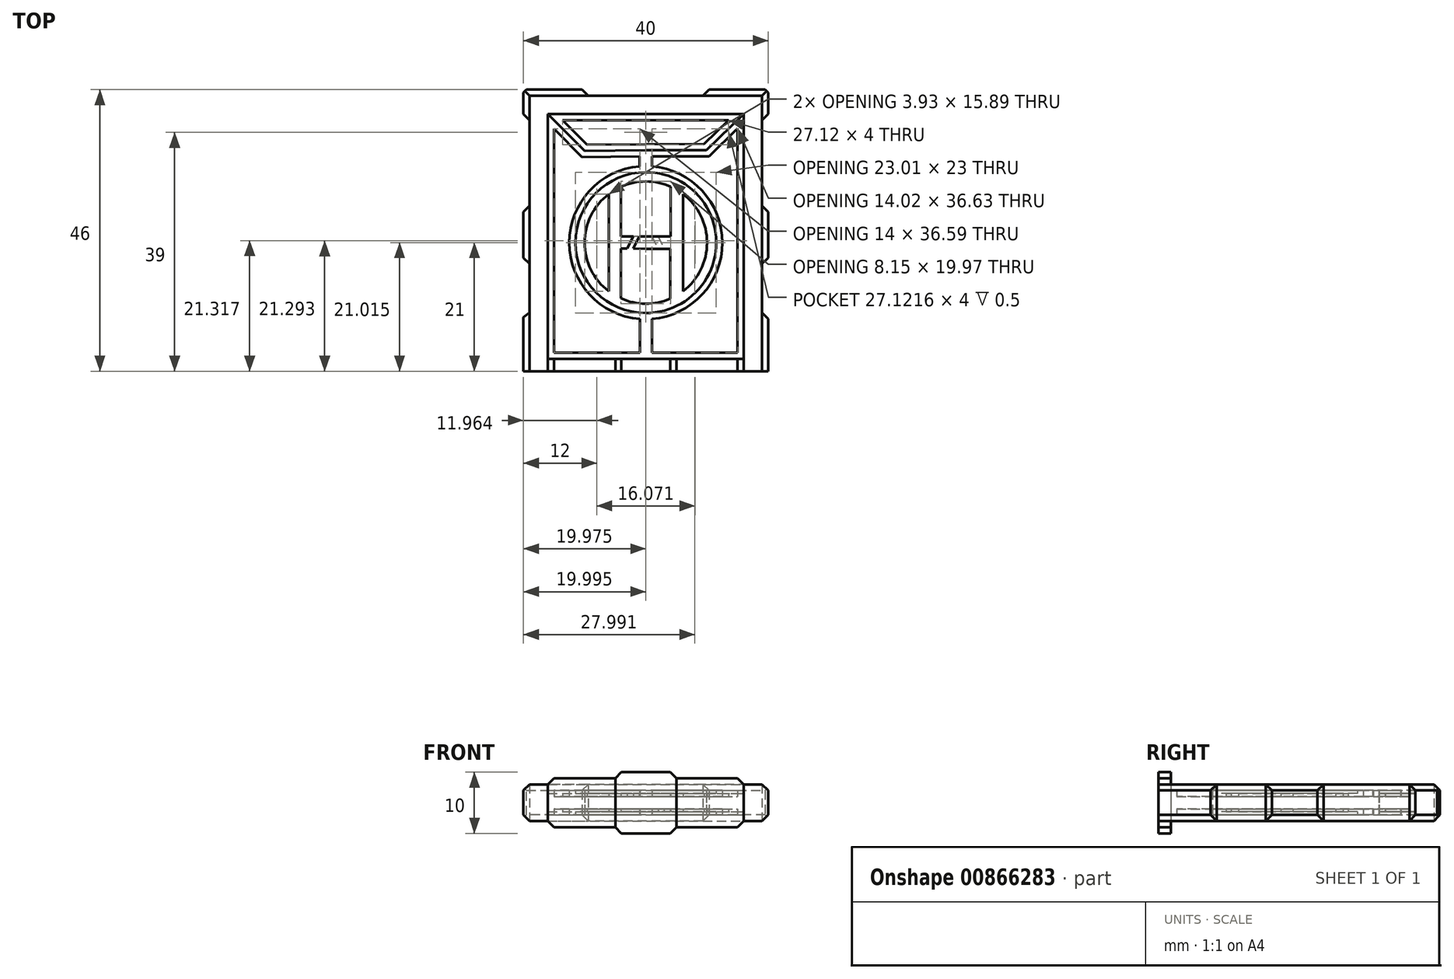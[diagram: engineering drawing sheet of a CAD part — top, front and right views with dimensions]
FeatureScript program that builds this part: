
annotation { "Feature Type Name" : "Feature", "Feature Type Description" : "" }
export const myFeature = defineFeature(function(context is Context, id is Id, definition is map)
    precondition{}
    {
        {
            var Q0;
            Q0=qCreatedBy(makeId("Top.planeOp"),FACE);
            var sketch = newSketch(context, id + "F0", { "sketchPlane" : qUnion([Q0])});
            skLineSegment(sketch, "E0.bottom", {"start": v(-16, 21) * mm, "end": v(16, 21) * mm});
            skPoint(sketch, "E0.middle", {"position": v(0, 0) * mm});
            skLineSegment(sketch, "E1", {"start": v(16, -21) * mm, "end": v(20, -21) * mm});
            skLineSegment(sketch, "E2", {"start": v(-16, -21) * mm, "end": v(-20, -21) * mm});
            skLineSegment(sketch, "E3", {"start": v(9.91, 15.09) * mm, "end": v(16, 21) * mm});
            skLineSegment(sketch, "E4", {"start": v(-16, 21) * mm, "end": v(-10, 15) * mm});
            skLineSegment(sketch, "E5", {"start": v(6.07, 1) * mm, "end": v(6.07, 7.95) * mm});
            skLineSegment(sketch, "E6", {"start": v(6.07, 1) * mm, "end": v(6.07, -7.95) * mm});
            skLineSegment(sketch, "E7", {"start": v(-6.07, 1) * mm, "end": v(-6.07, 7.95) * mm});
            skLineSegment(sketch, "E8", {"start": v(-6.07, 1) * mm, "end": v(-6.07, -7.95) * mm});
            skLineSegment(sketch, "E9", {"start": v(-4.07, 1) * mm, "end": v(-4.07, 9.13) * mm});
            skLineSegment(sketch, "E10", {"start": v(-4.08, -0.97) * mm, "end": v(-4.08, -9.13) * mm});
            skLineSegment(sketch, "E11", {"start": v(4.07, 1) * mm, "end": v(4.07, 9.13) * mm});
            skLineSegment(sketch, "E12", {"start": v(4, -1) * mm, "end": v(-0.08, -1) * mm});
            skLineSegment(sketch, "E13", {"start": v(4.07, 1) * mm, "end": v(0, 1) * mm});
            skLineSegment(sketch, "E14", {"start": v(4, -1) * mm, "end": v(4, -9.13) * mm});
            skLineSegment(sketch, "E15", {"start": v(-4.08, -0.97) * mm, "end": v(-3.08, -0.98) * mm});
            skLineSegment(sketch, "E16", {"start": v(-4.07, 1) * mm, "end": v(-2.08, 1) * mm});
            skLineSegment(sketch, "E17", {"start": v(-3.08, -0.98) * mm, "end": v(-2.08, 1) * mm});
            skLineSegment(sketch, "E18", {"start": v(-2.08, -0.98) * mm, "end": v(-1.08, 1) * mm});
            skLineSegment(sketch, "E19", {"start": v(-2.08, -0.98) * mm, "end": v(-0.08, -1) * mm});
            skLineSegment(sketch, "E20", {"start": v(-1.08, 1) * mm, "end": v(0, 1) * mm});
            skLineSegment(sketch, "E21.0", {"start": v(-13.59, 20) * mm, "end": v(-9.59, 16) * mm});
            skLineSegment(sketch, "E21.1", {"start": v(-13.59, 20) * mm, "end": v(13.54, 20) * mm});
            skLineSegment(sketch, "E21.2", {"start": v(9.51, 16.1) * mm, "end": v(13.54, 20) * mm});
            skLineSegment(sketch, "E21.3", {"start": v(-9.59, 16) * mm, "end": v(9.51, 16.1) * mm});
            skLineSegment(sketch, "E22", {"start": v(-0.02, 15.09) * mm, "end": v(-0.02, 11.5) * mm});
            skArc(sketch, "E23", {"start": v(-0.02, 11.5) * mm, "mid": v(11.5, 0) * mm, "end": v(0, -11.5) * mm});
            skArc(sketch, "E24", {"start": v(0, -11.5) * mm, "mid": v(-11.5, 0) * mm, "end": v(-0.02, 11.5) * mm});
            skLineSegment(sketch, "E25", {"start": v(-0.02, 15.09) * mm, "end": v(-10, 15) * mm});
            skLineSegment(sketch, "E26", {"start": v(-0.02, 15.09) * mm, "end": v(9.91, 15.09) * mm});
            skArc(sketch, "E27", {"start": v(-4.07, 9.13) * mm, "mid": v(0, 10) * mm, "end": v(4.07, 9.13) * mm});
            skArc(sketch, "E28", {"start": v(6.07, 7.95) * mm, "mid": v(10, 0) * mm, "end": v(6.07, -7.95) * mm});
            skArc(sketch, "E29", {"start": v(4, -9.13) * mm, "mid": v(-0.05, -9.97) * mm, "end": v(-4.08, -9.1) * mm});
            skArc(sketch, "E30", {"start": v(-6.07, -7.95) * mm, "mid": v(-10, 0) * mm, "end": v(-6.07, 7.95) * mm});
            skLineSegment(sketch, "E31", {"start": v(0, -11.5) * mm, "end": v(0, -19) * mm});
            skLineSegment(sketch, "E32", {"start": v(0, -19) * mm, "end": v(16, -19) * mm});
            skLineSegment(sketch, "E33", {"start": v(0, -19) * mm, "end": v(-16, -19) * mm});
            skLineSegment(sketch, "E34", {"start": v(16, -19) * mm, "end": v(16, -21) * mm});
            skLineSegment(sketch, "E35", {"start": v(16, -19) * mm, "end": v(16, 21) * mm});
            skLineSegment(sketch, "E36", {"start": v(-16, -21) * mm, "end": v(-16, -19) * mm});
            skLineSegment(sketch, "E37", {"start": v(-16, -19) * mm, "end": v(-16, 21) * mm});
            skLineSegment(sketch, "E38.0", {"start": v(1, -12.46) * mm, "end": v(1, -18) * mm});
            skArc(sketch, "E38.1", {"start": v(0.98, 12.46) * mm, "mid": v(12.5, 0) * mm, "end": v(1, -12.46) * mm});
            skLineSegment(sketch, "E38.2", {"start": v(15, -18) * mm, "end": v(15, 18.63) * mm});
            skLineSegment(sketch, "E38.3", {"start": v(10.32, 14.09) * mm, "end": v(15, 18.63) * mm});
            skLineSegment(sketch, "E38.4", {"start": v(0.98, 14.09) * mm, "end": v(10.32, 14.09) * mm});
            skLineSegment(sketch, "E38.5", {"start": v(1, -18) * mm, "end": v(15, -18) * mm});
            skLineSegment(sketch, "E38.6", {"start": v(0.98, 14.09) * mm, "end": v(0.98, 12.46) * mm});
            skLineSegment(sketch, "E39.0", {"start": v(-1, -12.46) * mm, "end": v(-1, -18) * mm});
            skArc(sketch, "E39.1", {"start": v(-1, -12.46) * mm, "mid": v(-12.5, 0) * mm, "end": v(-1.02, 12.46) * mm});
            skLineSegment(sketch, "E39.2", {"start": v(-15, -18) * mm, "end": v(-15, 18.59) * mm});
            skLineSegment(sketch, "E39.3", {"start": v(-15, 18.59) * mm, "end": v(-10.41, 14) * mm});
            skLineSegment(sketch, "E39.4", {"start": v(-1.02, 14.08) * mm, "end": v(-10.41, 14) * mm});
            skLineSegment(sketch, "E39.5", {"start": v(-1, -18) * mm, "end": v(-15, -18) * mm});
            skLineSegment(sketch, "E39.6", {"start": v(-1.02, 14.08) * mm, "end": v(-1.02, 12.46) * mm});
            skLineSegment(sketch, "E40", {"start": v(20, 25) * mm, "end": v(20, 21) * mm});
            skLineSegment(sketch, "E41", {"start": v(20, -12.46) * mm, "end": v(20, -21) * mm});
            skLineSegment(sketch, "E42", {"start": v(-20, -21) * mm, "end": v(-20, -12.2) * mm});
            skLineSegment(sketch, "E43", {"start": v(-20, 21) * mm, "end": v(-20, 25) * mm});
            skLineSegment(sketch, "E44", {"start": v(10.32, 25) * mm, "end": v(20, 25) * mm});
            skLineSegment(sketch, "E45", {"start": v(-10.41, 25) * mm, "end": v(-20, 25) * mm});
            skLineSegment(sketch, "E46", {"start": v(-10.41, 25) * mm, "end": v(-9.41, 24) * mm});
            skLineSegment(sketch, "E47", {"start": v(9.32, 24) * mm, "end": v(-9.41, 24) * mm});
            skLineSegment(sketch, "E48", {"start": v(9.32, 24) * mm, "end": v(10.32, 25) * mm});
            skLineSegment(sketch, "E49", {"start": v(20, 21) * mm, "end": v(19, 20) * mm});
            skLineSegment(sketch, "E50", {"start": v(19, -11.46) * mm, "end": v(20, -12.46) * mm});
            skLineSegment(sketch, "E51", {"start": v(-20, -12.2) * mm, "end": v(-19, -11.46) * mm});
            skLineSegment(sketch, "E52", {"start": v(-20, 21) * mm, "end": v(-19, 20) * mm});
            skLineSegment(sketch, "E53", {"start": v(19, -11.46) * mm, "end": v(19, -3.46) * mm});
            skLineSegment(sketch, "E54", {"start": v(20, -2.46) * mm, "end": v(19, -3.46) * mm});
            skLineSegment(sketch, "E55", {"start": v(20, 5) * mm, "end": v(19, 6) * mm});
            skLineSegment(sketch, "E56", {"start": v(20, -2.46) * mm, "end": v(20, 5) * mm});
            skLineSegment(sketch, "E57", {"start": v(19, 6) * mm, "end": v(19, 20) * mm});
            skLineSegment(sketch, "E58", {"start": v(-19, -11.46) * mm, "end": v(-19, -3.46) * mm});
            skLineSegment(sketch, "E59", {"start": v(-20, 5) * mm, "end": v(-19, 6) * mm});
            skLineSegment(sketch, "E60", {"start": v(-20, -2.46) * mm, "end": v(-19, -3.46) * mm});
            skLineSegment(sketch, "E61", {"start": v(-20, 5) * mm, "end": v(-20, -2.46) * mm});
            skLineSegment(sketch, "E62", {"start": v(-19, 6) * mm, "end": v(-19, 20) * mm});
            skLineSegment(sketch, "E63", {"start": v(-16, -21) * mm, "end": v(-14, -21) * mm});
            skLineSegment(sketch, "E64", {"start": v(14, -21) * mm, "end": v(16, -21) * mm});
            skLineSegment(sketch, "E65", {"start": v(-14, -21) * mm, "end": v(14, -21) * mm});
            skLineSegment(sketch, "E66", {"start": v(0, -21) * mm, "end": v(5, -21) * mm});
            skLineSegment(sketch, "E67", {"start": v(0, -21) * mm, "end": v(-5, -21) * mm});
            skLineSegment(sketch, "E68", {"start": v(-5, -21) * mm, "end": v(-5, -19) * mm});
            skLineSegment(sketch, "E69", {"start": v(5, -21) * mm, "end": v(5, -19) * mm});
            skLineSegment(sketch, "E70", {"start": v(-1.08, 1) * mm, "end": v(-2.08, 1) * mm});
            skLineSegment(sketch, "E71", {"start": v(-2.08, -0.98) * mm, "end": v(-3.08, -0.98) * mm});
            skLineSegment(sketch, "E72", {"start": v(4, -1) * mm, "end": v(3, -1) * mm});
            skLineSegment(sketch, "E73", {"start": v(3, -1) * mm, "end": v(2, -1) * mm});
            skLineSegment(sketch, "E74", {"start": v(2, 1) * mm, "end": v(3, -1) * mm});
            skLineSegment(sketch, "E75", {"start": v(2, -1) * mm, "end": v(1, -1) * mm});
            skLineSegment(sketch, "E76", {"start": v(1, 1) * mm, "end": v(2, -1) * mm});
            skSolve(sketch);
        }
        {
            var Q0;
            Q0=makeQuery(id+"F0.imprint","IMPRINT",FACE,{"disambiguationData":[TD([[makeQuery(id+"F0.imprint","IMPRINT",EDGE,{"derivedFrom":sQuery(id+"F0.wireOp",EDGE,"E0.bottom")}),1.0]])]});
            extrude(context, id + "F1", {"entities" : qUnion([Q0]), "endBound" : BoundingType.SYMMETRIC, "depth" : 6 * mm, "offsetDistance" : 25 * mm});
        }
        {
            var Q0;
            {var subQ1=sQuery(id+"F0.wireOp",EDGE,"E36");Q0=makeQuery(id+"F0.imprint","IMPRINT",FACE,{"disambiguationData":[TD([[makeQuery(id+"F0.imprint","IMPRINT",EDGE,{"derivedFrom":subQ1}),-1.0]])]});}
            extrude(context, id + "F2", {"entities" : qUnion([Q0]), "endBound" : BoundingType.SYMMETRIC, "depth" : 8 * mm, "offsetDistance" : 25 * mm});
        }
        {
            var Q0;
            {var subQ3=sQuery(id+"F0.wireOp",EDGE,"E34");Q0=makeQuery(id+"F0.imprint","IMPRINT",FACE,{"disambiguationData":[TD([[makeQuery(id+"F0.imprint","IMPRINT",EDGE,{"derivedFrom":subQ3}),-1.0]])]});}
            extrude(context, id + "F3", {"entities" : qUnion([Q0]), "endBound" : BoundingType.SYMMETRIC, "depth" : 8 * mm, "offsetDistance" : 25 * mm});
        }
        {
            var Q0;
            {var subQ2=sQuery(id+"F0.wireOp",EDGE,"E68");Q0=makeQuery(id+"F0.imprint","IMPRINT",FACE,{"disambiguationData":[TD([[makeQuery(id+"F0.imprint","IMPRINT",EDGE,{"derivedFrom":subQ2}),-1.0]])]});}
            extrude(context, id + "F4", {"entities" : qUnion([Q0]), "endBound" : BoundingType.SYMMETRIC, "depth" : 10 * mm, "offsetDistance" : 25 * mm});
        }
        {
            var Q0;
            Q0=makeQuery(id+"F0.imprint","IMPRINT",FACE,{"disambiguationData":[TD([[makeQuery(id+"F0.imprint","IMPRINT",EDGE,{"derivedFrom":sQuery(id+"F0.wireOp",EDGE,"E3")}),-1.0]])]});
            var Q1;
            Q1=makeQuery(id+"F0.imprint","IMPRINT",FACE,{"disambiguationData":[TD([[makeQuery(id+"F0.imprint","IMPRINT",EDGE,{"derivedFrom":sQuery(id+"F0.wireOp",EDGE,"E4")}),-1.0]])]});
            extrude(context, id + "F5", {"entities" : qUnion([Q0, Q1]), "endBound" : BoundingType.SYMMETRIC, "depth" : 4 * mm, "offsetDistance" : 25 * mm});
        }
        {
            var Q0;
            Q0=makeQuery(id+"F0.imprint","IMPRINT",FACE,{"disambiguationData":[TD([[makeQuery(id+"F0.imprint","IMPRINT",EDGE,{"derivedFrom":sQuery(id+"F0.wireOp",EDGE,"E0.bottom")}),-1.0]])]});
            extrude(context, id + "F6", {"entities" : qUnion([Q0]), "endBound" : BoundingType.SYMMETRIC, "depth" : 3 * mm, "offsetDistance" : 25 * mm});
        }
        {
            var Q0;
            Q0=makeQuery(id+"F0.imprint","IMPRINT",FACE,{"disambiguationData":[TD([[makeQuery(id+"F0.imprint","IMPRINT",EDGE,{"derivedFrom":sQuery(id+"F0.wireOp",EDGE,"E5")}),1.0]])]});
            extrude(context, id + "F7", {"entities" : qUnion([Q0]), "operationType" : NewBodyOperationType.ADD, "endBound" : BoundingType.SYMMETRIC, "depth" : 3 * mm, "offsetDistance" : 25 * mm});
        }
        {
            var Q0;
            Q0=makeQuery(id+"F0.imprint","IMPRINT",FACE,{"disambiguationData":[TD([[makeQuery(id+"F0.imprint","IMPRINT",EDGE,{"derivedFrom":sQuery(id+"F0.wireOp",EDGE,"E21.0")}),1.0]])]});
            extrude(context, id + "F8", {"entities" : qUnion([Q0]), "operationType" : NewBodyOperationType.ADD, "endBound" : BoundingType.SYMMETRIC, "depth" : 2 * mm, "offsetDistance" : 25 * mm});
        }
        {
            var Q0;
            Q0=makeQuery(id+"F0.imprint","IMPRINT",FACE,{"disambiguationData":[TD([[makeQuery(id+"F0.imprint","IMPRINT",EDGE,{"derivedFrom":sQuery(id+"F0.wireOp",EDGE,"E39.0")}),-1.0]])]});
            extrude(context, id + "F9", {"entities" : qUnion([Q0]), "operationType" : NewBodyOperationType.ADD, "endBound" : BoundingType.SYMMETRIC, "depth" : 2 * mm, "offsetDistance" : 25 * mm});
        }
        {
            var Q0;
            Q0=makeQuery(id+"F0.imprint","IMPRINT",FACE,{"disambiguationData":[TD([[makeQuery(id+"F0.imprint","IMPRINT",EDGE,{"derivedFrom":sQuery(id+"F0.wireOp",EDGE,"E38.0")}),1.0]])]});
            extrude(context, id + "F10", {"entities" : qUnion([Q0]), "operationType" : NewBodyOperationType.ADD, "endBound" : BoundingType.SYMMETRIC, "depth" : 2 * mm, "offsetDistance" : 25 * mm});
        }
        {
            var Q0;
            Q0=makeQuery(id+"F0.imprint","IMPRINT",FACE,{"disambiguationData":[TD([[makeQuery(id+"F0.imprint","IMPRINT",EDGE,{"derivedFrom":sQuery(id+"F0.wireOp",EDGE,"E7")}),1.0]])]});
            extrude(context, id + "F11", {"entities" : qUnion([Q0]), "operationType" : NewBodyOperationType.ADD, "endBound" : BoundingType.SYMMETRIC, "depth" : 2 * mm, "offsetDistance" : 25 * mm});
        }
        {
            var Q0;
            Q0=makeQuery(id+"F0.imprint","IMPRINT",FACE,{"disambiguationData":[TD([[makeQuery(id+"F0.imprint","IMPRINT",EDGE,{"derivedFrom":sQuery(id+"F0.wireOp",EDGE,"E9")}),-1.0]])]});
            extrude(context, id + "F12", {"entities" : qUnion([Q0]), "operationType" : NewBodyOperationType.ADD, "endBound" : BoundingType.SYMMETRIC, "depth" : 2 * mm, "offsetDistance" : 25 * mm});
        }
        {
            var Q0;
            Q0=makeQuery(id+"F0.imprint","IMPRINT",FACE,{"disambiguationData":[TD([[makeQuery(id+"F0.imprint","IMPRINT",EDGE,{"derivedFrom":sQuery(id+"F0.wireOp",EDGE,"E5")}),-1.0]])]});
            extrude(context, id + "F13", {"entities" : qUnion([Q0]), "operationType" : NewBodyOperationType.ADD, "endBound" : BoundingType.SYMMETRIC, "depth" : 2 * mm, "offsetDistance" : 25 * mm});
        }
        {
            var Q0;
            Q0=makeQuery(id+"F1.opExtrude","SWEPT_EDGE",EDGE,{"disambiguationData":[OSD([sQuery(id+"F0.wireOp",EDGE,"E40"),sQuery(id+"F0.wireOp",EDGE,"E44")])]});
            var Q1;
            Q1=makeQuery(id+"F1.opExtrude","SWEPT_EDGE",EDGE,{"disambiguationData":[OSD([sQuery(id+"F0.wireOp",EDGE,"E43"),sQuery(id+"F0.wireOp",EDGE,"E45")])]});
            chamfer(context, id + "F14", {"entities" : qUnion([Q0, Q1]), "width" : .5 * mm, "tangentPropagation" : true});
        }
        {
            var Q0;
            Q0=makeQuery(id+"F1.opExtrude","CAP_EDGE",EDGE,{"disambiguationData":[OSD([sQuery(id+"F0.wireOp",EDGE,"E40")])],"isStart":false});
            var Q1;
            Q1=makeQuery(id+"F1.opExtrude","CAP_EDGE",EDGE,{"disambiguationData":[OSD([sQuery(id+"F0.wireOp",EDGE,"E44")])],"isStart":false});
            var Q2;
            Q2=makeQuery(id+"F1.opExtrude","CAP_EDGE",EDGE,{"disambiguationData":[OSD([sQuery(id+"F0.wireOp",EDGE,"E56")])],"isStart":false});
            var Q3;
            Q3=makeQuery(id+"F1.opExtrude","CAP_EDGE",EDGE,{"disambiguationData":[OSD([sQuery(id+"F0.wireOp",EDGE,"E41")])],"isStart":false});
            var Q4;
            Q4=makeQuery(id+"F3.opExtrude","CAP_EDGE",EDGE,{"disambiguationData":[OSD([sQuery(id+"F0.wireOp",EDGE,"E34")])],"isStart":false});
            var Q5;
            Q5=makeQuery(id+"F4.opExtrude","CAP_EDGE",EDGE,{"disambiguationData":[OSD([sQuery(id+"F0.wireOp",EDGE,"E69")])],"isStart":false});
            var Q6;
            Q6=makeQuery(id+"F1.opExtrude","CAP_EDGE",EDGE,{"disambiguationData":[OSD([sQuery(id+"F0.wireOp",EDGE,"E45")])],"isStart":false});
            var Q7;
            Q7=makeQuery(id+"F1.opExtrude","CAP_EDGE",EDGE,{"disambiguationData":[OSD([sQuery(id+"F0.wireOp",EDGE,"E43")])],"isStart":false});
            var Q8;
            Q8=makeQuery(id+"F1.opExtrude","CAP_EDGE",EDGE,{"disambiguationData":[OSD([sQuery(id+"F0.wireOp",EDGE,"E61")])],"isStart":false});
            var Q9;
            Q9=makeQuery(id+"F1.opExtrude","CAP_EDGE",EDGE,{"disambiguationData":[OSD([sQuery(id+"F0.wireOp",EDGE,"E42")])],"isStart":false});
            var Q10;
            Q10=makeQuery(id+"F2.opExtrude","CAP_EDGE",EDGE,{"disambiguationData":[OSD([sQuery(id+"F0.wireOp",EDGE,"E36")])],"isStart":false});
            var Q11;
            Q11=makeQuery(id+"F4.opExtrude","CAP_EDGE",EDGE,{"disambiguationData":[OSD([sQuery(id+"F0.wireOp",EDGE,"E68")])],"isStart":false});
            var Q12;
            Q12=makeQuery(id+"F4.opExtrude","CAP_EDGE",EDGE,{"disambiguationData":[OSD([sQuery(id+"F0.wireOp",EDGE,"E69")])],"isStart":true});
            var Q13;
            Q13=makeQuery(id+"F3.opExtrude","CAP_EDGE",EDGE,{"disambiguationData":[OSD([sQuery(id+"F0.wireOp",EDGE,"E34")])],"isStart":true});
            var Q14;
            Q14=makeQuery(id+"F1.opExtrude","CAP_EDGE",EDGE,{"disambiguationData":[OSD([sQuery(id+"F0.wireOp",EDGE,"E41")])],"isStart":true});
            var Q15;
            Q15=makeQuery(id+"F1.opExtrude","CAP_EDGE",EDGE,{"disambiguationData":[OSD([sQuery(id+"F0.wireOp",EDGE,"E56")])],"isStart":true});
            var Q16;
            Q16=makeQuery(id+"F1.opExtrude","CAP_EDGE",EDGE,{"disambiguationData":[OSD([sQuery(id+"F0.wireOp",EDGE,"E40")])],"isStart":true});
            var Q17;
            Q17=makeQuery(id+"F1.opExtrude","CAP_EDGE",EDGE,{"disambiguationData":[OSD([sQuery(id+"F0.wireOp",EDGE,"E44")])],"isStart":true});
            var Q18;
            Q18=makeQuery(id+"F1.opExtrude","CAP_EDGE",EDGE,{"disambiguationData":[OSD([sQuery(id+"F0.wireOp",EDGE,"E45")])],"isStart":true});
            var Q19;
            Q19=makeQuery(id+"F1.opExtrude","CAP_EDGE",EDGE,{"disambiguationData":[OSD([sQuery(id+"F0.wireOp",EDGE,"E43")])],"isStart":true});
            var Q20;
            Q20=makeQuery(id+"F1.opExtrude","CAP_EDGE",EDGE,{"disambiguationData":[OSD([sQuery(id+"F0.wireOp",EDGE,"E61")])],"isStart":true});
            var Q21;
            Q21=makeQuery(id+"F1.opExtrude","CAP_EDGE",EDGE,{"disambiguationData":[OSD([sQuery(id+"F0.wireOp",EDGE,"E42")])],"isStart":true});
            var Q22;
            Q22=makeQuery(id+"F2.opExtrude","CAP_EDGE",EDGE,{"disambiguationData":[OSD([sQuery(id+"F0.wireOp",EDGE,"E36")])],"isStart":true});
            var Q23;
            Q23=makeQuery(id+"F4.opExtrude","CAP_EDGE",EDGE,{"disambiguationData":[OSD([sQuery(id+"F0.wireOp",EDGE,"E68")])],"isStart":true});
            chamfer(context, id + "F15", {"entities" : qUnion([Q0, Q1, Q2, Q3, Q4, Q5, Q6, Q7, Q8, Q9, Q10, Q11, Q12, Q13, Q14, Q15, Q16, Q17, Q18, Q19, Q20, Q21, Q22, Q23]), "width" : 1 * mm, "tangentPropagation" : true});
        }
        {
            var Q0;
            {var subQ0=sQuery(id+"F0.wireOp",EDGE,"E14");Q0=makeQuery(id+"F0.imprint","IMPRINT",FACE,{"disambiguationData":[TD([[makeQuery(id+"F0.imprint","IMPRINT",EDGE,{"derivedFrom":subQ0}),-1.0]])]});}
            extrude(context, id + "F16", {"entities" : qUnion([Q0]), "operationType" : NewBodyOperationType.ADD, "endBound" : BoundingType.SYMMETRIC, "depth" : 2 * mm, "offsetDistance" : 25 * mm});
        }
        {
            var Q0;
            Q0=makeQuery(id+"F0.imprint","IMPRINT",FACE,{"disambiguationData":[TD([[makeQuery(id+"F0.imprint","IMPRINT",EDGE,{"derivedFrom":sQuery(id+"F0.wireOp",EDGE,"E17")}),-1.0]])]});
            extrude(context, id + "F17", {"entities" : qUnion([Q0]), "operationType" : NewBodyOperationType.ADD, "oppositeDirection" : true, "depth" : 1.5 * mm, "offsetDistance" : 25 * mm, "hasSecondDirection" : true, "secondDirectionOppositeDirection" : false, "secondDirectionDepth" : 1 * mm});
        }
        {
            var Q0;
            Q0=makeQuery(id+"F0.imprint","IMPRINT",FACE,{"disambiguationData":[TD([[makeQuery(id+"F0.imprint","IMPRINT",EDGE,{"derivedFrom":sQuery(id+"F0.wireOp",EDGE,"E18")}),-1.0]])]});
            extrude(context, id + "F18", {"entities" : qUnion([Q0]), "operationType" : NewBodyOperationType.ADD, "endBound" : BoundingType.SYMMETRIC, "depth" : 3 * mm, "offsetDistance" : 25 * mm});
        }
        {
            var Q0;
            {var subQ0=sQuery(id+"F0.wireOp",EDGE,"E74");Q0=makeQuery(id+"F0.imprint","IMPRINT",FACE,{"disambiguationData":[TD([[makeQuery(id+"F0.imprint","IMPRINT",EDGE,{"derivedFrom":subQ0}),-1.0]])]});}
            extrude(context, id + "F19", {"entities" : qUnion([Q0]), "operationType" : NewBodyOperationType.ADD, "depth" : 1.5 * mm, "offsetDistance" : 25 * mm, "hasSecondDirection" : true, "secondDirectionOppositeDirection" : true, "secondDirectionDepth" : 1 * mm});
        }
    });
